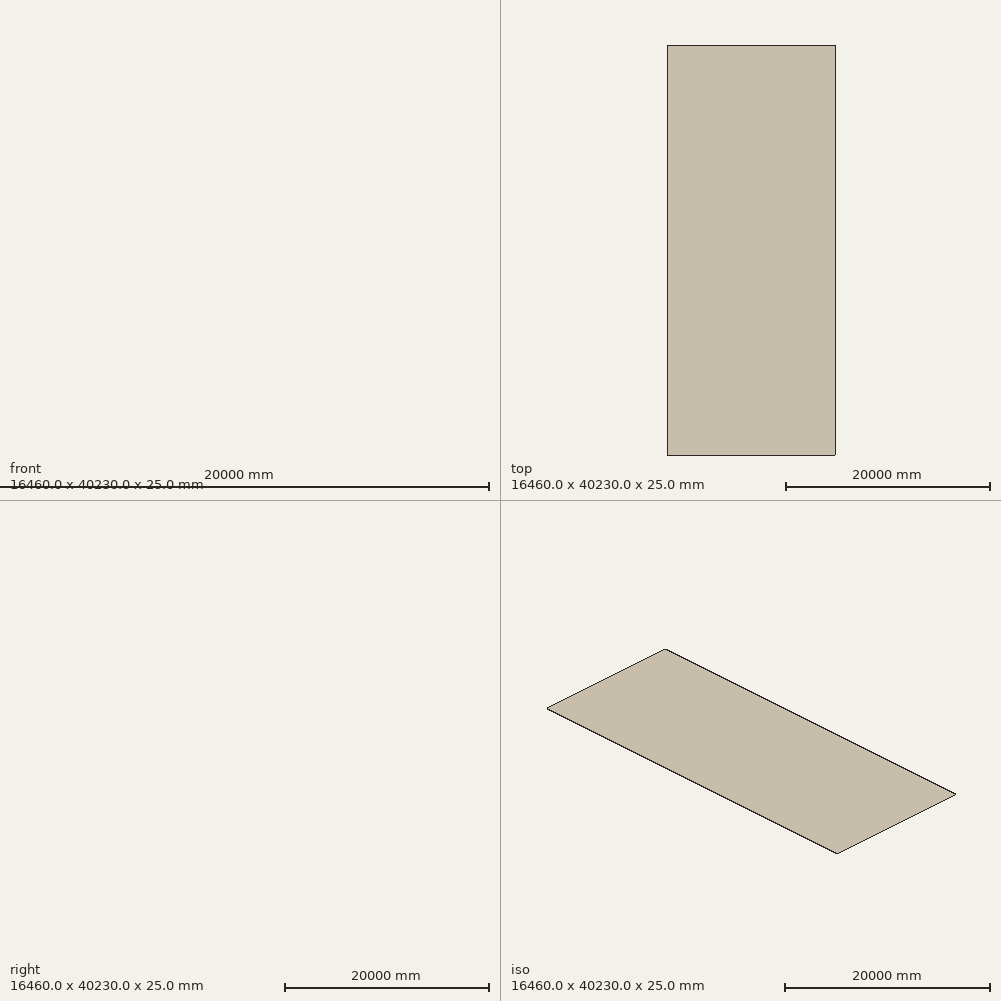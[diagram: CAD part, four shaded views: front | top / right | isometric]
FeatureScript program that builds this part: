
annotation { "Feature Type Name" : "Feature", "Feature Type Description" : "" }
export const myFeature = defineFeature(function(context is Context, id is Id, definition is map)
    precondition{}
    {
        {
            var Q0;
            Q0=qCreatedBy(makeId("Top.planeOp"),FACE);
            var sketch = newSketch(context, id + "F0", { "sketchPlane" : qUnion([Q0])});
            skLineSegment(sketch, "E0.bottom", {"start": v(8230, 20115) * mm, "end": v(-8230, 20115) * mm});
            skLineSegment(sketch, "E0.top", {"start": v(8230, -20115) * mm, "end": v(-8230, -20115) * mm});
            skLineSegment(sketch, "E0.left", {"start": v(8230, 20115) * mm, "end": v(8230, -20115) * mm});
            skLineSegment(sketch, "E0.right", {"start": v(-8230, 20115) * mm, "end": v(-8230, -20115) * mm});
            skPoint(sketch, "E0.middle", {"position": v(0, 0) * mm});
            skSolve(sketch);
        }
        {
            var Q0;
            Q0=makeQuery(id+"F0.imprint","IMPRINT",FACE,{"disambiguationData":[TD([[makeQuery(id+"F0.imprint","IMPRINT",EDGE,{"derivedFrom":sQuery(id+"F0.wireOp",EDGE,"E0.bottom")}),1.0]])]});
            extrude(context, id + "F1", {"entities" : qUnion([Q0]), "depth" : 25 * mm, "offsetDistance" : 25 * mm});
        }
    });
